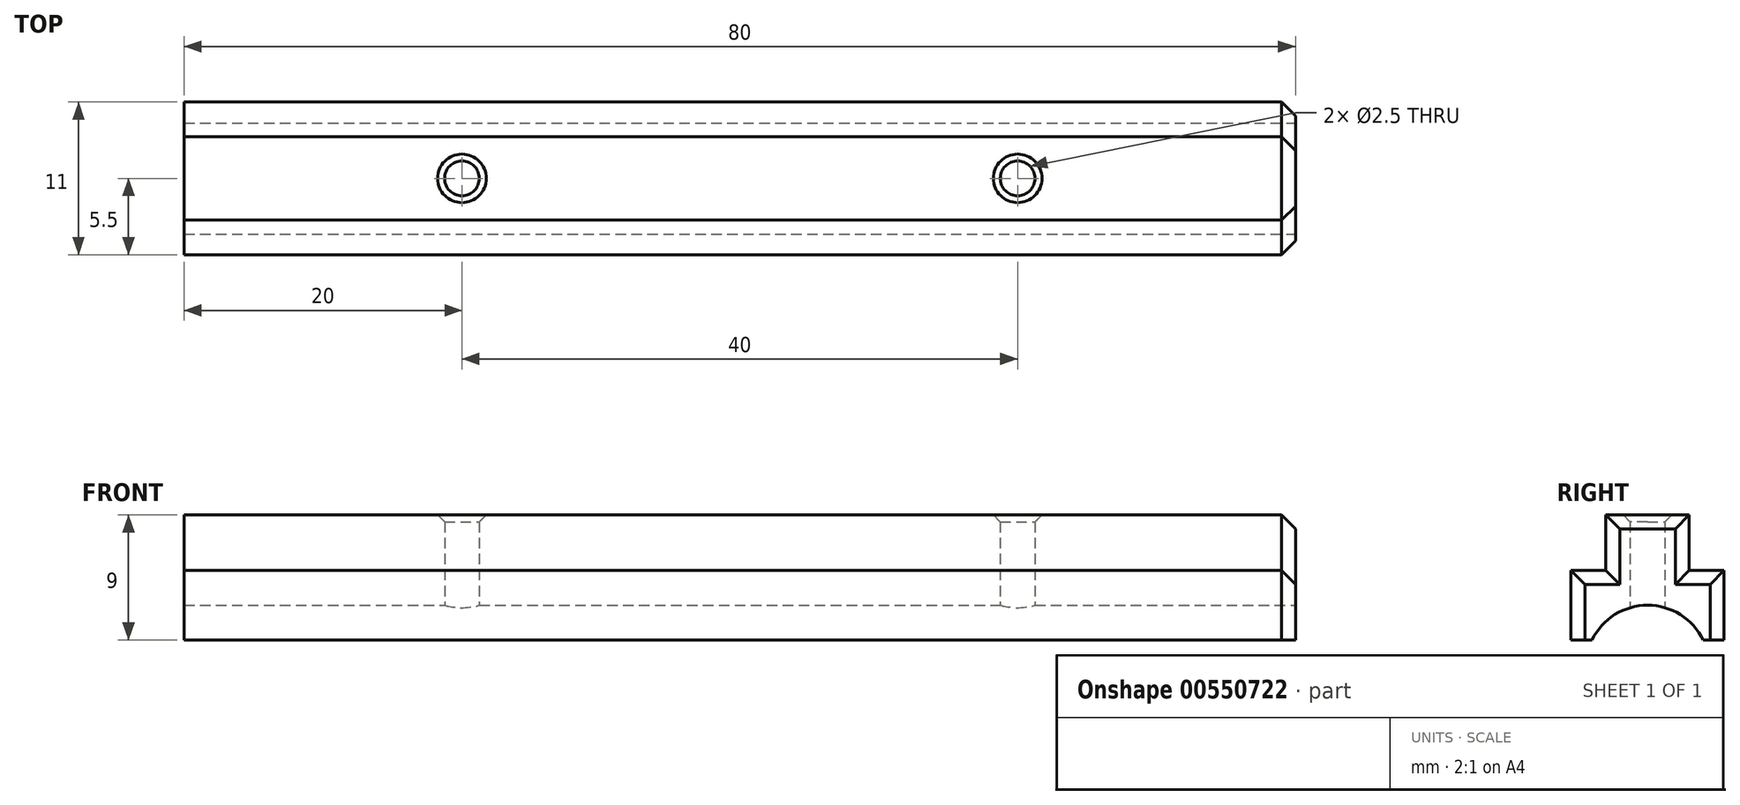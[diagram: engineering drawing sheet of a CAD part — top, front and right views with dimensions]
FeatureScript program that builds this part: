
annotation { "Feature Type Name" : "Feature", "Feature Type Description" : "" }
export const myFeature = defineFeature(function(context is Context, id is Id, definition is map)
    precondition{}
    {
        {
            var Q0;
            Q0=qCreatedBy(makeId("Top.planeOp"),FACE);
            var sketch = newSketch(context, id + "F0", { "sketchPlane" : qUnion([Q0])});
            skLineSegment(sketch, "E0.bottom", {"start": v(40, 5.5) * mm, "end": v(-40, 5.5) * mm});
            skLineSegment(sketch, "E0.top", {"start": v(40, -5.5) * mm, "end": v(-40, -5.5) * mm});
            skLineSegment(sketch, "E0.left", {"start": v(40, 5.5) * mm, "end": v(40, -5.5) * mm});
            skLineSegment(sketch, "E0.right", {"start": v(-40, 5.5) * mm, "end": v(-40, -5.5) * mm});
            skPoint(sketch, "E0.middle", {"position": v(0, 0) * mm});
            skLineSegment(sketch, "E1.bottom", {"start": v(40, 3) * mm, "end": v(-40, 3) * mm});
            skLineSegment(sketch, "E1.top", {"start": v(40, -3) * mm, "end": v(-40, -3) * mm});
            skLineSegment(sketch, "E1.left", {"start": v(40, 3) * mm, "end": v(40, -3) * mm});
            skLineSegment(sketch, "E1.right", {"start": v(-40, 3) * mm, "end": v(-40, -3) * mm});
            skCircle(sketch, "E2", {"center": v(-20, 0) * mm, "radius": 1.25 * mm});
            skCircle(sketch, "E3.MirrorC", {"center": v(20, 0) * mm, "radius": 1.25 * mm});
            skSolve(sketch);
        }
        {
            var Q0;
            {var subQ1=sQuery(id+"F0.wireOp",EDGE,"E1.bottom");Q0=makeQuery(id+"F0.imprint","IMPRINT",FACE,{"disambiguationData":[TD([[makeQuery(id+"F0.imprint","IMPRINT",EDGE,{"derivedFrom":subQ1}),1.0]])]});}
            extrude(context, id + "F1", {"entities" : qUnion([Q0]), "depth" : 9 * mm, "offsetDistance" : 25 * mm});
        }
        {
            var Q0;
            {var subQ0=sQuery(id+"F0.wireOp",EDGE,"E0.top");Q0=makeQuery(id+"F0.imprint","IMPRINT",FACE,{"disambiguationData":[TD([[makeQuery(id+"F0.imprint","IMPRINT",EDGE,{"derivedFrom":subQ0}),-1.0]])]});}
            var Q1;
            {var subQ0=sQuery(id+"F0.wireOp",EDGE,"E0.bottom");Q1=makeQuery(id+"F0.imprint","IMPRINT",FACE,{"disambiguationData":[TD([[makeQuery(id+"F0.imprint","IMPRINT",EDGE,{"derivedFrom":subQ0}),1.0]])]});}
            extrude(context, id + "F2", {"entities" : qUnion([Q0, Q1]), "operationType" : NewBodyOperationType.ADD, "depth" : 5 * mm, "offsetDistance" : 25 * mm});
        }
        {
            var Q0;
            {var subQ0=sQuery(id+"F0.wireOp",EDGE,"E0.left");Q0=makeQuery(id+"F2.boolean.opBoolean","MERGE",FACE,{"derivedFrom":[makeQuery(id+"F1.opExtrude","SWEPT_FACE",FACE,{"disambiguationData":[OSD([subQ0])]}),makeQuery(id+"F2.opExtrude","SWEPT_FACE",FACE,{"disambiguationData":[OSD([subQ0]),TDD([makeQuery(id+"F0.imprint","IMPRINT",EDGE,{"disambiguationData":[TD([[makeQuery(id+"F0.imprint","INTERSECT",VERTEX,{"derivedFrom":[sQuery(id+"F0.wireOp",EDGE,"E0.bottom"),subQ0]}),-1.0]])],"derivedFrom":subQ0})])]}),makeQuery(id+"F2.opExtrude","SWEPT_FACE",FACE,{"disambiguationData":[OSD([subQ0]),TDD([makeQuery(id+"F0.imprint","IMPRINT",EDGE,{"disambiguationData":[TD([[makeQuery(id+"F0.imprint","INTERSECT",VERTEX,{"derivedFrom":[sQuery(id+"F0.wireOp",EDGE,"E0.top"),subQ0]}),1.0]])],"derivedFrom":subQ0})])]})]});}
            var sketch = newSketch(context, id + "F3", { "sketchPlane" : qUnion([Q0])});
            skLineSegment(sketch, "E4", {"start": v(-5.5, 0) * mm, "end": v(-4, 0) * mm, "construction": true});
            skLineSegment(sketch, "E5.MirrorCS", {"start": v(5.5, 0) * mm, "end": v(4, 0) * mm, "construction": true});
            skArc(sketch, "E6", {"start": v(4, 0) * mm, "mid": v(0, 2.5) * mm, "end": v(-4, 0) * mm});
            skSolve(sketch);
        }
        {
            var Q0;
            {var subQ0=sQuery(id+"F3.wireOp",EDGE,"E6");Q0=makeQuery(id+"F3.imprint","IMPRINT",FACE,{"disambiguationData":[TD([[makeQuery(id+"F3.imprint","IMPRINT",EDGE,{"derivedFrom":subQ0}),1.0]])]});}
            extrude(context, id + "F4", {"entities" : qUnion([Q0]), "operationType" : NewBodyOperationType.REMOVE, "oppositeDirection" : true, "depth" : 80 * mm, "offsetDistance" : 25 * mm});
        }
        {
            var Q0;
            Q0=makeQuery(id+"F1.opExtrude","CAP_EDGE",EDGE,{"disambiguationData":[OSD([sQuery(id+"F0.wireOp",EDGE,"E2")])],"isStart":false});
            var Q1;
            Q1=makeQuery(id+"F1.opExtrude","CAP_EDGE",EDGE,{"disambiguationData":[OSD([sQuery(id+"F0.wireOp",EDGE,"E3.MirrorC")])],"isStart":false});
            chamfer(context, id + "F5", {"entities" : qUnion([Q0, Q1]), "width" : 0.5 * mm, "tangentPropagation" : true});
        }
        {
            var Q0;
            {var subQ0=sQuery(id+"F0.wireOp",EDGE,"E0.left");Q0=makeQuery(id+"F2.opExtrude","CAP_EDGE",EDGE,{"disambiguationData":[OSD([subQ0]),TDD([makeQuery(id+"F0.imprint","IMPRINT",EDGE,{"disambiguationData":[TD([[makeQuery(id+"F0.imprint","INTERSECT",VERTEX,{"derivedFrom":[sQuery(id+"F0.wireOp",EDGE,"E0.bottom"),subQ0]}),-1.0]])],"derivedFrom":subQ0})])],"isStart":false});}
            var Q1;
            Q1=makeQuery(id+"F2.opExtrude","SWEPT_EDGE",EDGE,{"disambiguationData":[OSD([sQuery(id+"F0.wireOp",EDGE,"E0.bottom"),sQuery(id+"F0.wireOp",EDGE,"E0.left")])]});
            var Q2;
            Q2=makeQuery(id+"F1.opExtrude","SWEPT_EDGE",EDGE,{"disambiguationData":[OSD([sQuery(id+"F0.wireOp",EDGE,"E0.left"),sQuery(id+"F0.wireOp",EDGE,"E1.bottom")])]});
            var Q3;
            Q3=makeQuery(id+"F1.opExtrude","CAP_EDGE",EDGE,{"disambiguationData":[OSD([sQuery(id+"F0.wireOp",EDGE,"E0.left")])],"isStart":false});
            var Q4;
            Q4=makeQuery(id+"F1.opExtrude","SWEPT_EDGE",EDGE,{"disambiguationData":[OSD([sQuery(id+"F0.wireOp",EDGE,"E0.left"),sQuery(id+"F0.wireOp",EDGE,"E1.top")])]});
            var Q5;
            {var subQ0=sQuery(id+"F0.wireOp",EDGE,"E0.left");Q5=makeQuery(id+"F2.opExtrude","CAP_EDGE",EDGE,{"disambiguationData":[OSD([subQ0]),TDD([makeQuery(id+"F0.imprint","IMPRINT",EDGE,{"disambiguationData":[TD([[makeQuery(id+"F0.imprint","INTERSECT",VERTEX,{"derivedFrom":[sQuery(id+"F0.wireOp",EDGE,"E0.top"),subQ0]}),1.0]])],"derivedFrom":subQ0})])],"isStart":false});}
            var Q6;
            Q6=makeQuery(id+"F2.opExtrude","SWEPT_EDGE",EDGE,{"disambiguationData":[OSD([sQuery(id+"F0.wireOp",EDGE,"E0.top"),sQuery(id+"F0.wireOp",EDGE,"E0.left")])]});
            chamfer(context, id + "F6", {"entities" : qUnion([Q0, Q1, Q2, Q3, Q4, Q5, Q6]), "width" : 1 * mm, "tangentPropagation" : true});
        }
    });
